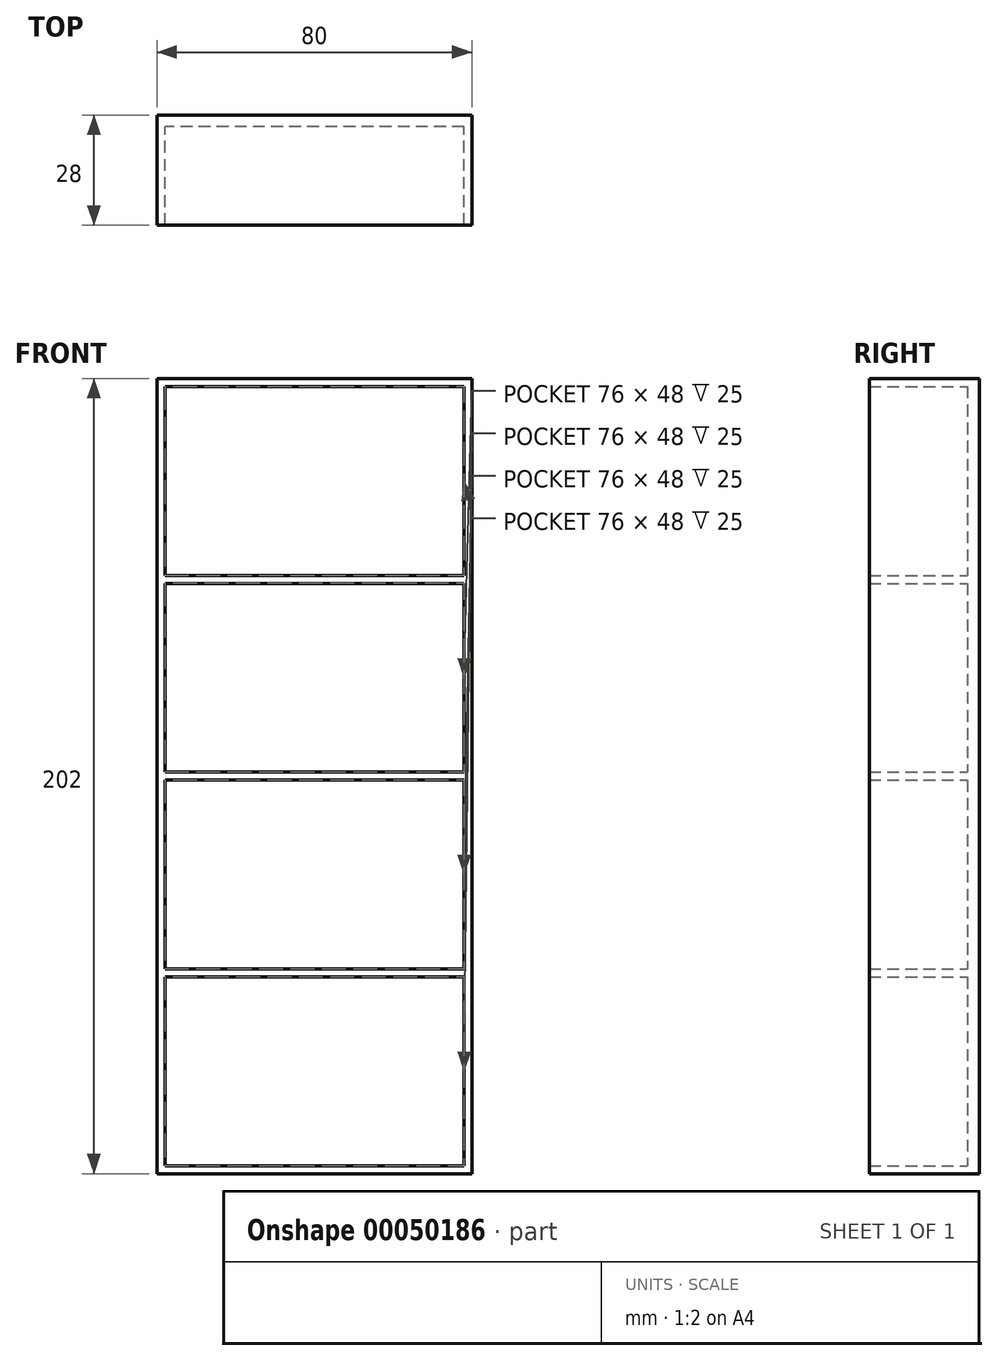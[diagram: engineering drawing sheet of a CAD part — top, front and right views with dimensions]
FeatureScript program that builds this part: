
annotation { "Feature Type Name" : "Feature", "Feature Type Description" : "" }
export const myFeature = defineFeature(function(context is Context, id is Id, definition is map)
    precondition{}
    {
        {
            var Q0;
            Q0=qCreatedBy(makeId("Front.planeOp"),FACE);
            var sketch = newSketch(context, id + "F0", { "sketchPlane" : qUnion([Q0])});
            skLineSegment(sketch, "E0.bottom", {"start": v(-53.42, 79.47) * mm, "end": v(26.58, 79.47) * mm});
            skLineSegment(sketch, "E0.top", {"start": v(-53.42, -122.53) * mm, "end": v(26.58, -122.53) * mm});
            skLineSegment(sketch, "E0.left", {"start": v(-53.42, 79.47) * mm, "end": v(-53.42, -122.53) * mm});
            skLineSegment(sketch, "E0.right", {"start": v(26.58, 79.47) * mm, "end": v(26.58, -122.53) * mm});
            skLineSegment(sketch, "E1.0", {"start": v(-51.42, 77.47) * mm, "end": v(24.58, 77.47) * mm});
            skLineSegment(sketch, "E1.1", {"start": v(-51.42, 77.47) * mm, "end": v(-51.42, 29.47) * mm});
            skLineSegment(sketch, "E1.2", {"start": v(-51.42, -120.53) * mm, "end": v(24.58, -120.53) * mm});
            skLineSegment(sketch, "E1.3", {"start": v(24.58, 77.47) * mm, "end": v(24.58, 29.47) * mm});
            skLineSegment(sketch, "E2.bottom", {"start": v(-51.42, -20.53) * mm, "end": v(24.58, -20.53) * mm});
            skLineSegment(sketch, "E2.top", {"start": v(-51.42, -22.53) * mm, "end": v(24.58, -22.53) * mm});
            skPoint(sketch, "E3.trimOffspring.end.orphan", {"position": v(-51.42, -21.53) * mm});
            skPoint(sketch, "E4.end.orphan", {"position": v(-47.7, -20.53) * mm});
            skPoint(sketch, "E5.end.orphan", {"position": v(-47.7, -22.53) * mm});
            skLineSegment(sketch, "E6.trimOffspring", {"start": v(-51.42, -22.53) * mm, "end": v(-51.42, -70.53) * mm});
            skPoint(sketch, "E7.start.orphan", {"position": v(24.58, -21.53) * mm});
            skLineSegment(sketch, "E8.trimOffspring", {"start": v(24.58, -22.53) * mm, "end": v(24.58, -70.53) * mm});
            skLineSegment(sketch, "E9", {"start": v(-36.23, 29.47) * mm, "end": v(24.58, 29.47) * mm});
            skLineSegment(sketch, "E10.MirrorCS", {"start": v(-36.23, 29.47) * mm, "end": v(-51.42, 29.47) * mm});
            skPoint(sketch, "E11.orphan", {"position": v(-51.42, 30.47) * mm});
            skPoint(sketch, "E12.MirrorCS.end.orphan", {"position": v(24.58, 30.47) * mm});
            skLineSegment(sketch, "E13.MirrorCS", {"start": v(-36.23, 27.47) * mm, "end": v(24.58, 27.47) * mm});
            skLineSegment(sketch, "E14.MirrorCS", {"start": v(-36.23, 27.47) * mm, "end": v(-51.42, 27.47) * mm});
            skPoint(sketch, "E15.orphan", {"position": v(-51.42, 28.47) * mm});
            skLineSegment(sketch, "E16.trimOffspring", {"start": v(-51.42, 27.47) * mm, "end": v(-51.42, -20.53) * mm});
            skPoint(sketch, "E17.end.orphan", {"position": v(24.58, 28.47) * mm});
            skLineSegment(sketch, "E18.trimOffspring", {"start": v(24.58, 27.47) * mm, "end": v(24.58, -20.53) * mm});
            skPoint(sketch, "E19.MirrorCS.start.orphan", {"position": v(-36.23, 29.47) * mm});
            skPoint(sketch, "E20.end.orphan", {"position": v(-51.42, 29.47) * mm});
            skLineSegment(sketch, "E21", {"start": v(-43.28, -70.53) * mm, "end": v(-51.42, -70.53) * mm});
            skLineSegment(sketch, "E22", {"start": v(-43.28, -70.53) * mm, "end": v(24.58, -70.53) * mm});
            skLineSegment(sketch, "E23.MirrorCS", {"start": v(-43.28, -72.53) * mm, "end": v(24.58, -72.53) * mm});
            skLineSegment(sketch, "E24.MirrorCS", {"start": v(-43.28, -72.53) * mm, "end": v(-51.42, -72.53) * mm});
            skPoint(sketch, "E25.start.orphan", {"position": v(24.58, -71.53) * mm});
            skPoint(sketch, "E26.trimOffspring.end.orphan", {"position": v(-51.42, -71.53) * mm});
            skLineSegment(sketch, "E27.trimOffspring", {"start": v(24.58, -72.53) * mm, "end": v(24.58, -120.53) * mm});
            skLineSegment(sketch, "E28", {"start": v(-51.42, -72.53) * mm, "end": v(-51.42, -120.53) * mm});
            skSolve(sketch);
        }
        {
            var Q0;
            Q0=makeQuery(id+"F0.imprint","IMPRINT",FACE,{"disambiguationData":[TD([[makeQuery(id+"F0.imprint","IMPRINT",EDGE,{"derivedFrom":sQuery(id+"F0.wireOp",EDGE,"E0.bottom")}),-1.0]])]});
            extrude(context, id + "F1", {"entities" : qUnion([Q0]), "depth" : 25 * mm});
        }
        {
            var Q0;
            Q0=makeQuery(id+"F1.opExtrude","CAP_FACE",FACE,{"disambiguationData":[OSD([sQuery(id+"F0.wireOp",EDGE,"E0.bottom"),sQuery(id+"F0.wireOp",EDGE,"E0.top"),sQuery(id+"F0.wireOp",EDGE,"E0.left"),sQuery(id+"F0.wireOp",EDGE,"E0.right"),sQuery(id+"F0.wireOp",EDGE,"E1.0"),sQuery(id+"F0.wireOp",EDGE,"E1.1"),sQuery(id+"F0.wireOp",EDGE,"E1.2"),sQuery(id+"F0.wireOp",EDGE,"E1.3"),sQuery(id+"F0.wireOp",EDGE,"E2.bottom"),sQuery(id+"F0.wireOp",EDGE,"E2.top"),sQuery(id+"F0.wireOp",EDGE,"E6.trimOffspring"),sQuery(id+"F0.wireOp",EDGE,"E8.trimOffspring"),sQuery(id+"F0.wireOp",EDGE,"E9"),sQuery(id+"F0.wireOp",EDGE,"E10.MirrorCS"),sQuery(id+"F0.wireOp",EDGE,"E13.MirrorCS"),sQuery(id+"F0.wireOp",EDGE,"E14.MirrorCS"),sQuery(id+"F0.wireOp",EDGE,"E16.trimOffspring"),sQuery(id+"F0.wireOp",EDGE,"E18.trimOffspring"),sQuery(id+"F0.wireOp",EDGE,"E21"),sQuery(id+"F0.wireOp",EDGE,"E22"),sQuery(id+"F0.wireOp",EDGE,"E23.MirrorCS"),sQuery(id+"F0.wireOp",EDGE,"E24.MirrorCS"),sQuery(id+"F0.wireOp",EDGE,"E27.trimOffspring"),sQuery(id+"F0.wireOp",EDGE,"E28")])],"isStart":true});
            var sketch = newSketch(context, id + "F2", { "sketchPlane" : qUnion([Q0])});
            skLineSegment(sketch, "E29.bottom", {"start": v(-26.58, 79.47) * mm, "end": v(53.42, 79.47) * mm});
            skLineSegment(sketch, "E29.top", {"start": v(-26.58, -122.53) * mm, "end": v(53.42, -122.53) * mm});
            skLineSegment(sketch, "E29.left", {"start": v(-26.58, 79.47) * mm, "end": v(-26.58, -122.53) * mm});
            skLineSegment(sketch, "E29.right", {"start": v(53.42, 79.47) * mm, "end": v(53.42, -122.53) * mm});
            skSolve(sketch);
        }
        {
            var Q0;
            Q0 = qSketchRegion(id + "F2", true);
            extrude(context, id + "F3", {"entities" : qUnion([Q0]), "operationType" : NewBodyOperationType.ADD, "depth" : 3 * mm});
        }
    });
